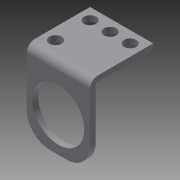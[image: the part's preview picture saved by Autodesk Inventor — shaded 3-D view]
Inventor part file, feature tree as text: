
AUTODESK INVENTOR PART (.ipt)
format: ipt  version: 2013 (Build 170138000, 138)  size: 212,480 bytes
history: native  units: in
note: dims shown in document units (in); Inventor stores cm internally (conversion verified against a paired STEP export)
features: other x6, sketch x5, sheet_metal_op x4, reference x1
ambient origin geometry x8: Origin, YZ Plane, XZ Plane, XY Plane, X Axis, Y Axis, Z Axis, Center Point
bodies: Solid1 (feature_tree)
feature tree (16):
  sheet_metal_op  "Face1"
  sheet_metal_op  "Flange1"
  sketch  "Sketch1"  dims[d0=1.3714in]
  other  "Plate1"
  sketch  "Sketch4"  dims[d2=1.25in]
  other  "Plate3"
  sheet_metal_op  "Bend2"
  sheet_metal_op  "Corner1"
  sketch  "Sketch5"  dims[d3=0.266in]
  sketch  "Sketch6"  dims[d4=0.266in]
  sketch  "Sketch7"  dims[d5=0.4357in d6=0.266in d7=0.4357in d8=0.25in d9=0.25in d10=0.25in d11=0.25in d12=0.125in d28=0.125in d29=0.0625in d30=0.25in d31=0.125in d32=1.75in d33=90.0deg d34=0.05in d35=0.5in d36=0.125in d37=0.125in d38=1.125in d39=0.125in d40=0.0in d41=0.75in d43=0.0in d44=1.0in d47=1.0in d48=0.125in d49=0.0in d50=0.125in d51=0.0in d1=0.125in]
  reference  "Reference1"
  other  "Cut1"
  other  "Cut2"
  other  "Cut3"
  other  "Definition1"
